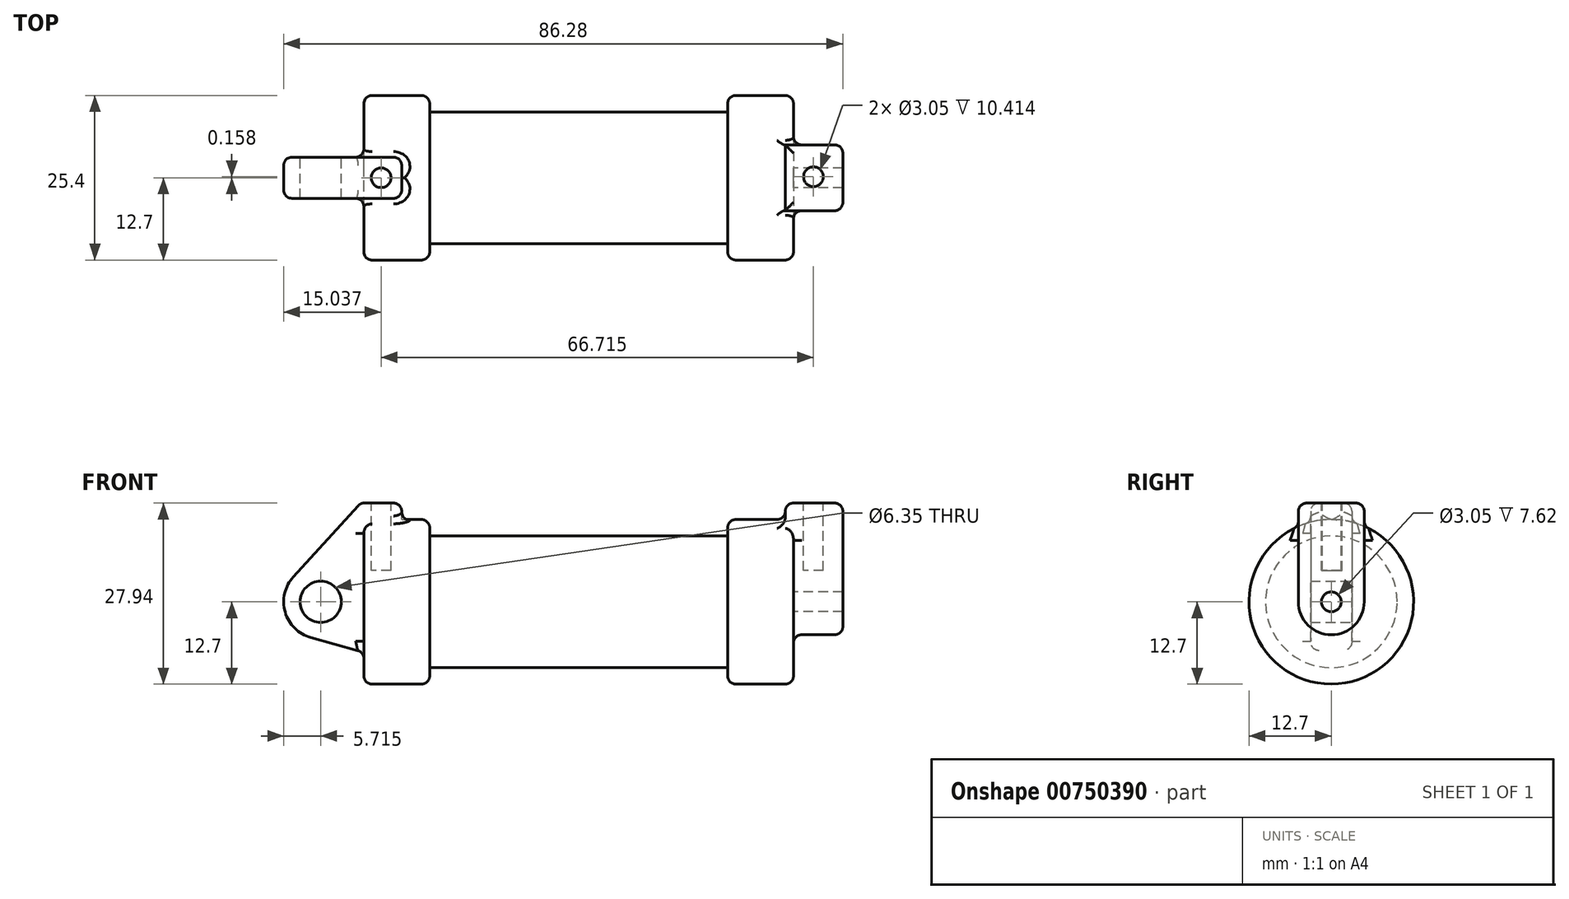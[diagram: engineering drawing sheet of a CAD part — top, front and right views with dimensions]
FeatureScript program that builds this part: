
annotation { "Feature Type Name" : "Feature", "Feature Type Description" : "" }
export const myFeature = defineFeature(function(context is Context, id is Id, definition is map)
    precondition{}
    {
        {
            var Q0;
            Q0=qCreatedBy(makeId("Front.planeOp"),FACE);
            var sketch = newSketch(context, id + "F0", { "sketchPlane" : qUnion([Q0])});
            skLineSegment(sketch, "E0", {"start": v(0, 0) * mm, "end": v(0, 12.7) * mm});
            skLineSegment(sketch, "E1", {"start": v(0, 12.7) * mm, "end": v(10.16, 12.7) * mm});
            skLineSegment(sketch, "E2", {"start": v(10.16, 12.7) * mm, "end": v(10.16, 10.16) * mm});
            skLineSegment(sketch, "E3", {"start": v(10.16, 10.16) * mm, "end": v(56.13, 10.16) * mm});
            skLineSegment(sketch, "E4", {"start": v(56.13, 10.16) * mm, "end": v(56.13, 12.7) * mm});
            skLineSegment(sketch, "E5", {"start": v(56.13, 12.7) * mm, "end": v(66.3, 12.7) * mm});
            skLineSegment(sketch, "E6", {"start": v(66.3, 12.7) * mm, "end": v(66.3, 0) * mm});
            skLineSegment(sketch, "E7", {"start": v(66.3, 0) * mm, "end": v(0, 0) * mm});
            skLineSegment(sketch, "E8", {"start": v(5.84, 15.24) * mm, "end": v(-0.5, 15.24) * mm});
            skLineSegment(sketch, "E9", {"start": v(-0.5, 15.24) * mm, "end": v(-10.88, 3.85) * mm});
            skLineSegment(sketch, "E10", {"start": v(0, 0) * mm, "end": v(-6.65, 0) * mm});
            skCircle(sketch, "E11", {"center": v(-6.65, 0) * mm, "radius": 5.72 * mm});
            skCircle(sketch, "E12", {"center": v(-6.65, 0) * mm, "radius": 3.18 * mm});
            skLineSegment(sketch, "E13", {"start": v(5.84, 15.24) * mm, "end": v(5.84, -9.4) * mm});
            skLineSegment(sketch, "E14", {"start": v(5.84, -9.4) * mm, "end": v(-8.18, -5.5) * mm});
            skSolve(sketch);
        }
        {
            var Q0;
            {var subQ0=sQuery(id+"F0.wireOp",EDGE,"E2");Q0=makeQuery(id+"F0.imprint","IMPRINT",FACE,{"disambiguationData":[TD([[makeQuery(id+"F0.imprint","IMPRINT",EDGE,{"derivedFrom":subQ0}),-1.0]])]});}
            var Q1;
            {var subQ0=sQuery(id+"F0.wireOp",EDGE,"E0");Q1=makeQuery(id+"F0.imprint","IMPRINT",FACE,{"disambiguationData":[TD([[makeQuery(id+"F0.imprint","IMPRINT",EDGE,{"derivedFrom":subQ0}),-1.0]])]});}
            var Q2;
            Q2=sQuery(id+"F0.wireOp",EDGE,"E7");
            revolve(context, id + "F1", {"surfaceOperationType" : NewSurfaceOperationType.NEW, "entities" : qUnion([Q0, Q1]), "axis" : qUnion([Q2]), "revolveType" : RevolveType.FULL});
        }
        {
            var Q0;
            {var subQ1=sQuery(id+"F0.wireOp",EDGE,"E0");Q0=makeQuery(id+"F0.imprint","IMPRINT",FACE,{"disambiguationData":[TD([[makeQuery(id+"F0.imprint","IMPRINT",EDGE,{"derivedFrom":subQ1}),1.0]])]});}
            var Q1;
            {var subQ0=sQuery(id+"F0.wireOp",EDGE,"E0");Q1=makeQuery(id+"F0.imprint","IMPRINT",FACE,{"disambiguationData":[TD([[makeQuery(id+"F0.imprint","IMPRINT",EDGE,{"derivedFrom":subQ0}),-1.0]])]});}
            var Q2;
            {var subQ5=sQuery(id+"F0.wireOp",EDGE,"E12");Q2=makeQuery(id+"F0.imprint","IMPRINT",FACE,{"disambiguationData":[TD([[makeQuery(id+"F0.imprint","IMPRINT",EDGE,{"derivedFrom":subQ5}),-1.0]])]});}
            var Q3;
            {var subQ0=sQuery(id+"F0.wireOp",EDGE,"E14");Q3=makeQuery(id+"F0.imprint","IMPRINT",FACE,{"disambiguationData":[TD([[makeQuery(id+"F0.imprint","IMPRINT",EDGE,{"derivedFrom":subQ0}),-1.0]])]});}
            extrude(context, id + "F2", {"entities" : qUnion([Q0, Q1, Q2, Q3]), "operationType" : NewBodyOperationType.ADD, "endBound" : BoundingType.SYMMETRIC, "depth" : 6.35 * mm, "offsetDistance" : 25.4 * mm});
        }
        {
            var Q0;
            Q0=makeQuery(id+"F1.opRevolve","SWEPT_FACE",FACE,{"disambiguationData":[OSD([sQuery(id+"F0.wireOp",EDGE,"E6")])]});
            var sketch = newSketch(context, id + "F3", { "sketchPlane" : qUnion([Q0])});
            skCircle(sketch, "E15", {"center": v(0, 0) * mm, "radius": 1.52 * mm});
            skCircle(sketch, "E16", {"center": v(0, 0) * mm, "radius": 5.08 * mm});
            skLineSegment(sketch, "E17", {"start": v(-5.08, 0) * mm, "end": v(-5.08, 15.24) * mm});
            skLineSegment(sketch, "E18", {"start": v(5.08, 0) * mm, "end": v(5.08, 15.24) * mm});
            skLineSegment(sketch, "E19", {"start": v(5.08, 15.24) * mm, "end": v(-5.08, 15.24) * mm});
            skSolve(sketch);
        }
        {
            var Q0;
            {var subQ0=sQuery(id+"F3.wireOp",EDGE,"E17");var subQ1=sQuery(id+"F3.wireOp",EDGE,"E16");var subQ2=makeQuery(id+"F3.imprint","INTERSECT",VERTEX,{"derivedFrom":[subQ1,subQ0]});Q0=makeQuery(id+"F3.imprint","IMPRINT",FACE,{"disambiguationData":[TD([[makeQuery(id+"F3.imprint","IMPRINT",EDGE,{"disambiguationData":[TD([[subQ2,1.0]])],"derivedFrom":subQ1}),-1.0]])]});}
            var Q1;
            Q1=makeQuery(id+"F3.imprint","IMPRINT",FACE,{"disambiguationData":[TD([[makeQuery(id+"F3.imprint","IMPRINT",EDGE,{"derivedFrom":sQuery(id+"F3.wireOp",EDGE,"E15")}),-1.0]])]});
            var Q2;
            {var subQ0=sQuery(id+"F3.wireOp",EDGE,"E19");Q2=makeQuery(id+"F3.imprint","IMPRINT",FACE,{"disambiguationData":[TD([[makeQuery(id+"F3.imprint","IMPRINT",EDGE,{"derivedFrom":subQ0}),1.0]])]});}
            extrude(context, id + "F4", {"entities" : qUnion([Q0, Q1, Q2]), "operationType" : NewBodyOperationType.ADD, "depth" : 7.62 * mm, "offsetDistance" : 25.4 * mm, "hasSecondDirection" : true, "secondDirectionOppositeDirection" : true, "secondDirectionDepth" : 1.27 * mm});
        }
        {
            var Q0;
            Q0=makeQuery(id+"F2.opExtrude","SWEPT_FACE",FACE,{"disambiguationData":[OSD([sQuery(id+"F0.wireOp",EDGE,"E8")])]});
            var sketch = newSketch(context, id + "F5", { "sketchPlane" : qUnion([Q0])});
            skCircle(sketch, "E20", {"center": v(2.67, 0) * mm, "radius": 1.52 * mm});
            skCircle(sketch, "E21", {"center": v(69.38, 0.16) * mm, "radius": 1.52 * mm});
            skSolve(sketch);
        }
        {
            var Q0;
            Q0=makeQuery(id+"F5.imprint","IMPRINT",FACE,{"disambiguationData":[TD([[makeQuery(id+"F5.imprint","IMPRINT",EDGE,{"derivedFrom":sQuery(id+"F5.wireOp",EDGE,"E20")}),1.0]])]});
            var Q1;
            Q1=makeQuery(id+"F5.imprint","IMPRINT",FACE,{"disambiguationData":[TD([[makeQuery(id+"F5.imprint","IMPRINT",EDGE,{"derivedFrom":sQuery(id+"F5.wireOp",EDGE,"E21")}),1.0]])]});
            extrude(context, id + "F6", {"entities" : qUnion([Q0, Q1]), "operationType" : NewBodyOperationType.REMOVE, "oppositeDirection" : true, "depth" : 10.4 * mm, "offsetDistance" : 25.4 * mm});
        }
        {
            var Q0;
            Q0=makeQuery(id+"F1.opRevolve","SWEPT_EDGE",EDGE,{"disambiguationData":[OSD([sQuery(id+"F0.wireOp",EDGE,"E1"),sQuery(id+"F0.wireOp",EDGE,"E2")])]});
            var Q1;
            Q1=makeQuery(id+"F1.opRevolve","SWEPT_EDGE",EDGE,{"disambiguationData":[OSD([sQuery(id+"F0.wireOp",EDGE,"E0"),sQuery(id+"F0.wireOp",EDGE,"E1")])]});
            var Q2;
            Q2=makeQuery(id+"F1.opRevolve","SWEPT_EDGE",EDGE,{"disambiguationData":[OSD([sQuery(id+"F0.wireOp",EDGE,"E4"),sQuery(id+"F0.wireOp",EDGE,"E5")])]});
            var Q3;
            Q3=makeQuery(id+"F1.opRevolve","SWEPT_EDGE",EDGE,{"disambiguationData":[OSD([sQuery(id+"F0.wireOp",EDGE,"E5"),sQuery(id+"F0.wireOp",EDGE,"E6")])]});
            fillet(context, id + "F7", {"entities" : qUnion([Q0, Q1, Q2, Q3]), "radius" : 1.27 * mm, "allowEdgeOverflow" : false});
        }
        {
            var Q0;
            Q0=makeQuery(id+"F4.boolean.opBoolean","INTERSECT",EDGE,{"derivedFrom":[makeQuery(id+"F1.opRevolve","SWEPT_FACE",FACE,{"disambiguationData":[OSD([sQuery(id+"F0.wireOp",EDGE,"E6")])]}),makeQuery(id+"F4.opExtrude","SWEPT_FACE",FACE,{"disambiguationData":[OSD([sQuery(id+"F3.wireOp",EDGE,"E17")])]})]});
            var Q1;
            Q1=makeQuery(id+"F4.opExtrude","CAP_EDGE",EDGE,{"disambiguationData":[OSD([sQuery(id+"F3.wireOp",EDGE,"E18")])],"isStart":false});
            var Q2;
            Q2=makeQuery(id+"F4.opExtrude","CAP_EDGE",EDGE,{"disambiguationData":[OSD([sQuery(id+"F3.wireOp",EDGE,"E19")])],"isStart":false});
            var Q3;
            Q3=makeQuery(id+"F4.opExtrude","SWEPT_EDGE",EDGE,{"disambiguationData":[OSD([sQuery(id+"F3.wireOp",EDGE,"E18"),sQuery(id+"F3.wireOp",EDGE,"E19")])]});
            var Q4;
            Q4=makeQuery(id+"F4.opExtrude","CAP_EDGE",EDGE,{"disambiguationData":[OSD([sQuery(id+"F3.wireOp",EDGE,"E19")])],"isStart":true});
            var Q5;
            Q5=makeQuery(id+"F4.opExtrude","SWEPT_EDGE",EDGE,{"disambiguationData":[OSD([sQuery(id+"F3.wireOp",EDGE,"E17"),sQuery(id+"F3.wireOp",EDGE,"E19")])]});
            var Q6;
            Q6=makeQuery(id+"F4.boolean.opBoolean","INTERSECT",EDGE,{"derivedFrom":[makeQuery(id+"F1.opRevolve","SWEPT_FACE",FACE,{"disambiguationData":[OSD([sQuery(id+"F0.wireOp",EDGE,"E5")])]}),makeQuery(id+"F4.opExtrude","CAP_FACE",FACE,{"disambiguationData":[OSD([sQuery(id+"F3.wireOp",EDGE,"E15"),sQuery(id+"F3.wireOp",EDGE,"E16"),sQuery(id+"F3.wireOp",EDGE,"E17"),sQuery(id+"F3.wireOp",EDGE,"E18"),sQuery(id+"F3.wireOp",EDGE,"E19")])],"isStart":true})]});
            fillet(context, id + "F8", {"entities" : qUnion([Q0, Q1, Q2, Q3, Q4, Q5, Q6]), "radius" : 1.27 * mm, "tangentPropagation" : true, "allowEdgeOverflow" : false});
        }
        {
            var Q0;
            Q0=makeQuery(id+"F2.opExtrude","CAP_EDGE",EDGE,{"disambiguationData":[OSD([sQuery(id+"F0.wireOp",EDGE,"E9")])],"isStart":true});
            var Q1;
            Q1=makeQuery(id+"F2.opExtrude","CAP_EDGE",EDGE,{"disambiguationData":[OSD([sQuery(id+"F0.wireOp",EDGE,"E8")])],"isStart":true});
            var Q2;
            Q2=makeQuery(id+"F2.opExtrude","CAP_EDGE",EDGE,{"disambiguationData":[OSD([sQuery(id+"F0.wireOp",EDGE,"E13")])],"isStart":true});
            var Q3;
            Q3=makeQuery(id+"F2.boolean.opBoolean","INTERSECT",EDGE,{"derivedFrom":[makeQuery(id+"F1.opRevolve","SWEPT_FACE",FACE,{"disambiguationData":[OSD([sQuery(id+"F0.wireOp",EDGE,"E1")])]}),makeQuery(id+"F2.opExtrude","CAP_FACE",FACE,{"disambiguationData":[OSD([sQuery(id+"F0.wireOp",EDGE,"E8"),sQuery(id+"F0.wireOp",EDGE,"E9"),sQuery(id+"F0.wireOp",EDGE,"E11"),sQuery(id+"F0.wireOp",EDGE,"E12"),sQuery(id+"F0.wireOp",EDGE,"E13"),sQuery(id+"F0.wireOp",EDGE,"E14")])],"isStart":true})]});
            var Q4;
            Q4=makeQuery(id+"F2.opExtrude","SWEPT_EDGE",EDGE,{"disambiguationData":[OSD([sQuery(id+"F0.wireOp",EDGE,"E9"),sQuery(id+"F0.wireOp",EDGE,"E11")])]});
            var Q5;
            Q5=makeQuery(id+"F2.opExtrude","CAP_EDGE",EDGE,{"disambiguationData":[OSD([sQuery(id+"F0.wireOp",EDGE,"E9")])],"isStart":false});
            var Q6;
            Q6=makeQuery(id+"F2.opExtrude","SWEPT_EDGE",EDGE,{"disambiguationData":[OSD([sQuery(id+"F0.wireOp",EDGE,"E8"),sQuery(id+"F0.wireOp",EDGE,"E9")])]});
            var Q7;
            Q7=makeQuery(id+"F2.opExtrude","CAP_EDGE",EDGE,{"disambiguationData":[OSD([sQuery(id+"F0.wireOp",EDGE,"E11")])],"isStart":true});
            var Q8;
            Q8=makeQuery(id+"F2.opExtrude","SWEPT_EDGE",EDGE,{"disambiguationData":[OSD([sQuery(id+"F0.wireOp",EDGE,"E11"),sQuery(id+"F0.wireOp",EDGE,"E14")])]});
            var Q9;
            Q9=makeQuery(id+"F2.opExtrude","CAP_EDGE",EDGE,{"disambiguationData":[OSD([sQuery(id+"F0.wireOp",EDGE,"E11")])],"isStart":false});
            var Q10;
            Q10=makeQuery(id+"F2.opExtrude","CAP_EDGE",EDGE,{"disambiguationData":[OSD([sQuery(id+"F0.wireOp",EDGE,"E14")])],"isStart":true});
            var Q11;
            Q11=makeQuery(id+"F2.boolean.opBoolean","INTERSECT",EDGE,{"derivedFrom":[makeQuery(id+"F1.opRevolve","SWEPT_FACE",FACE,{"disambiguationData":[OSD([sQuery(id+"F0.wireOp",EDGE,"E0")])]}),makeQuery(id+"F2.opExtrude","SWEPT_FACE",FACE,{"disambiguationData":[OSD([sQuery(id+"F0.wireOp",EDGE,"E14")])]})]});
            var Q12;
            Q12=makeQuery(id+"F2.opExtrude","CAP_EDGE",EDGE,{"disambiguationData":[OSD([sQuery(id+"F0.wireOp",EDGE,"E14")])],"isStart":false});
            var Q13;
            {var subQ0=sQuery(id+"F0.wireOp",EDGE,"E0");Q13=makeQuery(id+"F7.opFillet","BLEND_EDGE",EDGE,{"blendedFrom":[makeQuery(id+"F1.opRevolve","SWEPT_EDGE",EDGE,{"disambiguationData":[OSD([subQ0,sQuery(id+"F0.wireOp",EDGE,"E1")])]}),makeQuery(id+"F1.opRevolve","SWEPT_FACE",FACE,{"disambiguationData":[OSD([subQ0])]})],"blendedInto":[makeQuery(id+"F1.opRevolve","SWEPT_FACE",FACE,{"disambiguationData":[OSD([subQ0])]})]});}
            var Q14;
            Q14=makeQuery(id+"F2.opExtrude","SWEPT_EDGE",EDGE,{"disambiguationData":[OSD([sQuery(id+"F0.wireOp",EDGE,"E8"),sQuery(id+"F0.wireOp",EDGE,"E13")])]});
            var Q15;
            Q15=makeQuery(id+"F2.opExtrude","CAP_EDGE",EDGE,{"disambiguationData":[OSD([sQuery(id+"F0.wireOp",EDGE,"E8")])],"isStart":false});
            var Q16;
            Q16=makeQuery(id+"F2.boolean.opBoolean","INTERSECT",EDGE,{"derivedFrom":[makeQuery(id+"F1.opRevolve","SWEPT_FACE",FACE,{"disambiguationData":[OSD([sQuery(id+"F0.wireOp",EDGE,"E0")])]}),makeQuery(id+"F2.opExtrude","CAP_FACE",FACE,{"disambiguationData":[OSD([sQuery(id+"F0.wireOp",EDGE,"E8"),sQuery(id+"F0.wireOp",EDGE,"E9"),sQuery(id+"F0.wireOp",EDGE,"E11"),sQuery(id+"F0.wireOp",EDGE,"E12"),sQuery(id+"F0.wireOp",EDGE,"E13"),sQuery(id+"F0.wireOp",EDGE,"E14")])],"isStart":true})]});
            var Q17;
            Q17=makeQuery(id+"F7.opFillet","BLEND_EDGE",EDGE,{"blendedFrom":[makeQuery(id+"F1.opRevolve","SWEPT_EDGE",EDGE,{"disambiguationData":[OSD([sQuery(id+"F0.wireOp",EDGE,"E0"),sQuery(id+"F0.wireOp",EDGE,"E1")])]}),makeQuery(id+"F2.opExtrude","CAP_FACE",FACE,{"disambiguationData":[OSD([sQuery(id+"F0.wireOp",EDGE,"E8"),sQuery(id+"F0.wireOp",EDGE,"E9"),sQuery(id+"F0.wireOp",EDGE,"E11"),sQuery(id+"F0.wireOp",EDGE,"E12"),sQuery(id+"F0.wireOp",EDGE,"E13"),sQuery(id+"F0.wireOp",EDGE,"E14")])],"isStart":true})],"blendedInto":[makeQuery(id+"F2.opExtrude","CAP_FACE",FACE,{"disambiguationData":[OSD([sQuery(id+"F0.wireOp",EDGE,"E8"),sQuery(id+"F0.wireOp",EDGE,"E9"),sQuery(id+"F0.wireOp",EDGE,"E11"),sQuery(id+"F0.wireOp",EDGE,"E12"),sQuery(id+"F0.wireOp",EDGE,"E13"),sQuery(id+"F0.wireOp",EDGE,"E14")])],"isStart":true})]});
            var Q18;
            Q18=makeQuery(id+"F2.boolean.opBoolean","INTERSECT",EDGE,{"derivedFrom":[makeQuery(id+"F1.opRevolve","SWEPT_FACE",FACE,{"disambiguationData":[OSD([sQuery(id+"F0.wireOp",EDGE,"E1")])]}),makeQuery(id+"F2.opExtrude","CAP_FACE",FACE,{"disambiguationData":[OSD([sQuery(id+"F0.wireOp",EDGE,"E8"),sQuery(id+"F0.wireOp",EDGE,"E9"),sQuery(id+"F0.wireOp",EDGE,"E11"),sQuery(id+"F0.wireOp",EDGE,"E12"),sQuery(id+"F0.wireOp",EDGE,"E13"),sQuery(id+"F0.wireOp",EDGE,"E14")])],"isStart":false})]});
            var Q19;
            Q19=makeQuery(id+"F7.opFillet","BLEND_EDGE",EDGE,{"blendedFrom":[makeQuery(id+"F1.opRevolve","SWEPT_EDGE",EDGE,{"disambiguationData":[OSD([sQuery(id+"F0.wireOp",EDGE,"E0"),sQuery(id+"F0.wireOp",EDGE,"E1")])]}),makeQuery(id+"F2.opExtrude","CAP_FACE",FACE,{"disambiguationData":[OSD([sQuery(id+"F0.wireOp",EDGE,"E8"),sQuery(id+"F0.wireOp",EDGE,"E9"),sQuery(id+"F0.wireOp",EDGE,"E11"),sQuery(id+"F0.wireOp",EDGE,"E12"),sQuery(id+"F0.wireOp",EDGE,"E13"),sQuery(id+"F0.wireOp",EDGE,"E14")])],"isStart":false})],"blendedInto":[makeQuery(id+"F2.opExtrude","CAP_FACE",FACE,{"disambiguationData":[OSD([sQuery(id+"F0.wireOp",EDGE,"E8"),sQuery(id+"F0.wireOp",EDGE,"E9"),sQuery(id+"F0.wireOp",EDGE,"E11"),sQuery(id+"F0.wireOp",EDGE,"E12"),sQuery(id+"F0.wireOp",EDGE,"E13"),sQuery(id+"F0.wireOp",EDGE,"E14")])],"isStart":false})]});
            var Q20;
            Q20=makeQuery(id+"F2.boolean.opBoolean","INTERSECT",EDGE,{"derivedFrom":[makeQuery(id+"F1.opRevolve","SWEPT_FACE",FACE,{"disambiguationData":[OSD([sQuery(id+"F0.wireOp",EDGE,"E0")])]}),makeQuery(id+"F2.opExtrude","CAP_FACE",FACE,{"disambiguationData":[OSD([sQuery(id+"F0.wireOp",EDGE,"E8"),sQuery(id+"F0.wireOp",EDGE,"E9"),sQuery(id+"F0.wireOp",EDGE,"E11"),sQuery(id+"F0.wireOp",EDGE,"E12"),sQuery(id+"F0.wireOp",EDGE,"E13"),sQuery(id+"F0.wireOp",EDGE,"E14")])],"isStart":false})]});
            var Q21;
            Q21=makeQuery(id+"F2.opExtrude","CAP_EDGE",EDGE,{"disambiguationData":[OSD([sQuery(id+"F0.wireOp",EDGE,"E13")])],"isStart":false});
            var Q22;
            {var subQ0=sQuery(id+"F0.wireOp",EDGE,"E1");Q22=makeQuery(id+"F7.opFillet","BLEND_EDGE",EDGE,{"blendedFrom":[makeQuery(id+"F1.opRevolve","SWEPT_EDGE",EDGE,{"disambiguationData":[OSD([sQuery(id+"F0.wireOp",EDGE,"E0"),subQ0])]}),makeQuery(id+"F1.opRevolve","SWEPT_FACE",FACE,{"disambiguationData":[OSD([subQ0])]})],"blendedInto":[makeQuery(id+"F1.opRevolve","SWEPT_FACE",FACE,{"disambiguationData":[OSD([subQ0])]})]});}
            fillet(context, id + "F9", {"entities" : qUnion([Q0, Q1, Q2, Q3, Q4, Q5, Q6, Q7, Q8, Q9, Q10, Q11, Q12, Q13, Q14, Q15, Q16, Q17, Q18, Q19, Q20, Q21, Q22]), "radius" : 1.27 * mm, "tangentPropagation" : true, "allowEdgeOverflow" : false});
        }
    });
